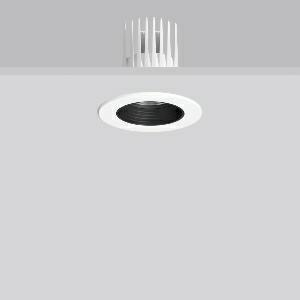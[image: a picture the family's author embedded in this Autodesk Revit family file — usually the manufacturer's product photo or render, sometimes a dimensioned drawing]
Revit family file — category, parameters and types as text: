
# Revit family: heledon_mini_e_901743_002_9522
name_source: partatom
category: Lighting Fixtures
units: mm (PartAtom-declared; Revit-internal decimal feet)

## family parameters
Cut with Voids When Loaded = No
Host = Face
Light Source = No
Part Type = Normal
Room Calculation Point = No
Round Connector Dimension = Use Diameter
Shared = No

## types (1)
- HELEDON mini E (1 x LED Modul 930, 2250 lm, 3000)
    Apparent Load = 20 VA
    Approval mark = CE
    CIE Flux Codes = 99 100 100 100 100
    Color Rendering = 90
    Color Temperature = 3000
    Default Elevation = 1800 mm
    Description = Series: HELEDON mini
Round recessed downlight. Housing: die-cast aluminium, powder-coated. Black plastic ring and recessed LED to prevent glare from the side. Optical assembly with lens made of plastic (polycarbonate) for the best homogeneous light distribution - can be changed without tools. Best colour rendering index Ra>90. Suitable for Recessed ceiling mounting. Installation without tools thanks to spring fastening system. Including separate LED converter with connecting cable 600 mm.High quality converter without flickering and stroboscopic effect. Through-wiring box (5 pole) available as accessory. The following accessories can be mounted without use of tools: interchangeable lenses, decorative glasses, honeycomb louvre, clear and frosted diffusers, white interchangeable plastic ring. 
Colour: traffic white, matt (RAL 9016)
Diameter: 124 mm
Height: 3 mm
Cut-out diameter: 114 mm
Recess height: 170 mm
Luminaire: recess height: 120 mm
Lamp: LED
Socket: without socket
Colour temperature: 3000K
Colour rendering index (CRI): 92
System power: 20 W
Rated luminous flux: 2250 lm
Luminous efficiency: 113 lm/W
Control gear: Regulated power supply
Protection class: II
Type of protection: IP 20
    Height = 0 mm  [stored 0 ft]
    Lamp = 1 x LED Modul 930
    Lamp Light Flux = 2250 lm
    Lamp count = 1
    Length = 124 mm  [stored 0.406824 ft]
    Lifetime = 50000 h
    Luminous efficacy = 113 lm/W
    Manufacturer = RZB
    ModVariant = No
    Model = 901743.002
    Mounting Place = Ceiling
    Mounting Type = Recessed
    Number of Poles = 1
    OnlyDefault = Yes
    Power Factor = 1
    Product Name = HELEDON mini E
    Product group = Recessed downlights
    ProductGroupID = 402
    Protection Class = Protection class II
    Protection Degree = IP 20
    RLX_Detail_Level = 1
    RLX_Emergency_Light_Flux = 0 lm
    RLX_Emergency_Type = 0
    RLX_Emergency_Type_DB = No
    RlxData = <blob elided: 124557 chars, md5=6b87412d>
    Socket = socket
    Standby Power = 0 W
    System Light Flux = 2250 lm
    System Power = 20 W
    Type Comments = Product without accessories
    Type Image = 901656.002.jpg
    URL = http://relux.com
    VarID = ---
    Voltage = 230 V
    Voltage Range = 220-240 V
    Weight = 0.00 kg
    Width = 0 mm  [stored 0 ft]

note: [stored X ft] marks values corroborated as IEEE doubles in the binary element streams (Revit-internal decimal feet)

## geometry (parser evidence)
native form markers: Blend x4, Sweep x11
no freeform markers — native parametric forms only
